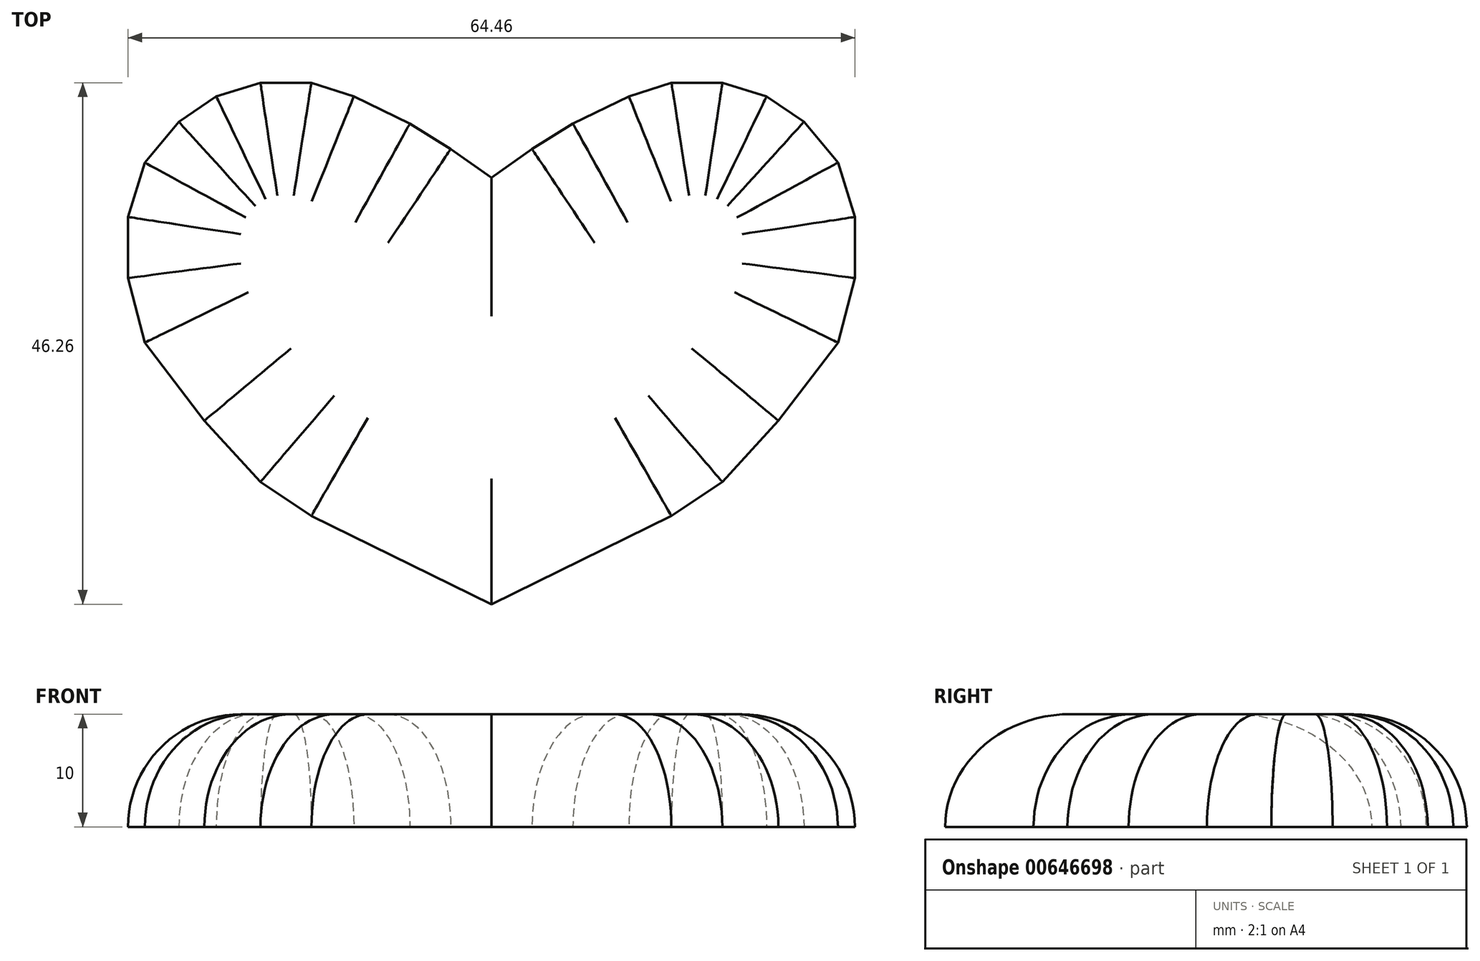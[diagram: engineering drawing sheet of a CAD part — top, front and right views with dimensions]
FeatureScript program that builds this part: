
annotation { "Feature Type Name" : "Feature", "Feature Type Description" : "" }
export const myFeature = defineFeature(function(context is Context, id is Id, definition is map)
    precondition{}
    {
        {
            var Q0;
            Q0=qCreatedBy(makeId("Top.planeOp"),FACE);
            var sketch = newSketch(context, id + "F0", { "sketchPlane" : qUnion([Q0])});
            skLineSegment(sketch, "E0", {"start": v(0, -24.58) * mm, "end": v(15.96, -16.75) * mm});
            skLineSegment(sketch, "E1", {"start": v(15.96, -16.75) * mm, "end": v(20.48, -13.73) * mm});
            skLineSegment(sketch, "E2", {"start": v(20.48, -13.73) * mm, "end": v(25.45, -8.31) * mm});
            skLineSegment(sketch, "E3", {"start": v(25.45, -8.31) * mm, "end": v(30.73, -1.38) * mm});
            skLineSegment(sketch, "E4", {"start": v(30.73, -1.38) * mm, "end": v(32.23, 4.35) * mm});
            skLineSegment(sketch, "E5", {"start": v(32.23, 4.35) * mm, "end": v(32.23, 9.77) * mm});
            skLineSegment(sketch, "E6", {"start": v(32.23, 9.77) * mm, "end": v(30.73, 14.6) * mm});
            skLineSegment(sketch, "E7", {"start": v(30.73, 14.6) * mm, "end": v(27.71, 18.2) * mm});
            skLineSegment(sketch, "E8", {"start": v(27.71, 18.2) * mm, "end": v(24.4, 20.47) * mm});
            skLineSegment(sketch, "E9", {"start": v(24.4, 20.47) * mm, "end": v(20.48, 21.68) * mm});
            skLineSegment(sketch, "E10", {"start": v(20.48, 21.68) * mm, "end": v(15.96, 21.68) * mm});
            skLineSegment(sketch, "E11", {"start": v(15.96, 21.68) * mm, "end": v(12.2, 20.47) * mm});
            skLineSegment(sketch, "E12", {"start": v(12.2, 20.47) * mm, "end": v(7.22, 18.06) * mm});
            skLineSegment(sketch, "E13", {"start": v(7.22, 18.06) * mm, "end": v(3.6, 15.8) * mm});
            skLineSegment(sketch, "E14", {"start": v(3.6, 15.8) * mm, "end": v(0, 13.24) * mm});
            skLineSegment(sketch, "E15", {"start": v(0, 13.24) * mm, "end": v(0, -24.58) * mm});
            skSolve(sketch);
        }
        {
            var Q0;
            Q0 = qSketchRegion(id + "F0", true);
            extrude(context, id + "F1", {"entities" : qUnion([Q0]), "depth" : 10 * mm, "offsetDistance" : 25.4 * mm});
        }
        {
            var Q0;
            Q0=makeQuery(id+"F1.opExtrude","SWEPT_BODY",BODY,{"disambiguationData":[OSD([sQuery(id+"F0.wireOp",EDGE,"E0"),sQuery(id+"F0.wireOp",EDGE,"E1"),sQuery(id+"F0.wireOp",EDGE,"E2"),sQuery(id+"F0.wireOp",EDGE,"E3"),sQuery(id+"F0.wireOp",EDGE,"E4"),sQuery(id+"F0.wireOp",EDGE,"E5"),sQuery(id+"F0.wireOp",EDGE,"E6"),sQuery(id+"F0.wireOp",EDGE,"E7"),sQuery(id+"F0.wireOp",EDGE,"E8"),sQuery(id+"F0.wireOp",EDGE,"E9"),sQuery(id+"F0.wireOp",EDGE,"E10"),sQuery(id+"F0.wireOp",EDGE,"E11"),sQuery(id+"F0.wireOp",EDGE,"E12"),sQuery(id+"F0.wireOp",EDGE,"E13"),sQuery(id+"F0.wireOp",EDGE,"E14"),sQuery(id+"F0.wireOp",EDGE,"E15")])]});
            var Q1;
            Q1=qCreatedBy(makeId("Right.planeOp"),FACE);
            mirror(context, id + "F2", {"operationType" : NewBodyOperationType.ADD, "entities" : qUnion([Q0]), "mirrorPlane" : qUnion([Q1])});
        }
        {
            var Q0;
            Q0=makeQuery(id+"F2.opPattern","COPY",EDGE,{"derivedFrom":makeQuery(id+"F1.opExtrude","CAP_EDGE",EDGE,{"disambiguationData":[OSD([sQuery(id+"F0.wireOp",EDGE,"E0")])],"isStart":false}),"instanceName":"1"});
            var Q1;
            Q1=makeQuery(id+"F1.opExtrude","CAP_EDGE",EDGE,{"disambiguationData":[OSD([sQuery(id+"F0.wireOp",EDGE,"E0")])],"isStart":false});
            var Q2;
            Q2=makeQuery(id+"F1.opExtrude","CAP_EDGE",EDGE,{"disambiguationData":[OSD([sQuery(id+"F0.wireOp",EDGE,"E1")])],"isStart":false});
            var Q3;
            Q3=makeQuery(id+"F1.opExtrude","CAP_EDGE",EDGE,{"disambiguationData":[OSD([sQuery(id+"F0.wireOp",EDGE,"E2")])],"isStart":false});
            var Q4;
            Q4=makeQuery(id+"F1.opExtrude","CAP_EDGE",EDGE,{"disambiguationData":[OSD([sQuery(id+"F0.wireOp",EDGE,"E3")])],"isStart":false});
            var Q5;
            Q5=makeQuery(id+"F1.opExtrude","CAP_EDGE",EDGE,{"disambiguationData":[OSD([sQuery(id+"F0.wireOp",EDGE,"E4")])],"isStart":false});
            var Q6;
            Q6=makeQuery(id+"F1.opExtrude","CAP_EDGE",EDGE,{"disambiguationData":[OSD([sQuery(id+"F0.wireOp",EDGE,"E5")])],"isStart":false});
            var Q7;
            Q7=makeQuery(id+"F1.opExtrude","CAP_EDGE",EDGE,{"disambiguationData":[OSD([sQuery(id+"F0.wireOp",EDGE,"E6")])],"isStart":false});
            var Q8;
            Q8=makeQuery(id+"F1.opExtrude","CAP_EDGE",EDGE,{"disambiguationData":[OSD([sQuery(id+"F0.wireOp",EDGE,"E7")])],"isStart":false});
            var Q9;
            Q9=makeQuery(id+"F1.opExtrude","CAP_EDGE",EDGE,{"disambiguationData":[OSD([sQuery(id+"F0.wireOp",EDGE,"E8")])],"isStart":false});
            var Q10;
            Q10=makeQuery(id+"F1.opExtrude","CAP_EDGE",EDGE,{"disambiguationData":[OSD([sQuery(id+"F0.wireOp",EDGE,"E9")])],"isStart":false});
            var Q11;
            Q11=makeQuery(id+"F1.opExtrude","CAP_EDGE",EDGE,{"disambiguationData":[OSD([sQuery(id+"F0.wireOp",EDGE,"E10")])],"isStart":false});
            var Q12;
            Q12=makeQuery(id+"F1.opExtrude","CAP_EDGE",EDGE,{"disambiguationData":[OSD([sQuery(id+"F0.wireOp",EDGE,"E11")])],"isStart":false});
            var Q13;
            Q13=makeQuery(id+"F1.opExtrude","CAP_EDGE",EDGE,{"disambiguationData":[OSD([sQuery(id+"F0.wireOp",EDGE,"E12")])],"isStart":false});
            var Q14;
            Q14=makeQuery(id+"F1.opExtrude","CAP_EDGE",EDGE,{"disambiguationData":[OSD([sQuery(id+"F0.wireOp",EDGE,"E14")])],"isStart":false});
            var Q15;
            Q15=makeQuery(id+"F1.opExtrude","CAP_EDGE",EDGE,{"disambiguationData":[OSD([sQuery(id+"F0.wireOp",EDGE,"E13")])],"isStart":false});
            var Q16;
            Q16=makeQuery(id+"F2.opPattern","COPY",EDGE,{"derivedFrom":makeQuery(id+"F1.opExtrude","CAP_EDGE",EDGE,{"disambiguationData":[OSD([sQuery(id+"F0.wireOp",EDGE,"E14")])],"isStart":false}),"instanceName":"1"});
            var Q17;
            Q17=makeQuery(id+"F2.opPattern","COPY",EDGE,{"derivedFrom":makeQuery(id+"F1.opExtrude","CAP_EDGE",EDGE,{"disambiguationData":[OSD([sQuery(id+"F0.wireOp",EDGE,"E13")])],"isStart":false}),"instanceName":"1"});
            var Q18;
            Q18=makeQuery(id+"F2.opPattern","COPY",EDGE,{"derivedFrom":makeQuery(id+"F1.opExtrude","CAP_EDGE",EDGE,{"disambiguationData":[OSD([sQuery(id+"F0.wireOp",EDGE,"E12")])],"isStart":false}),"instanceName":"1"});
            var Q19;
            Q19=makeQuery(id+"F2.opPattern","COPY",EDGE,{"derivedFrom":makeQuery(id+"F1.opExtrude","CAP_EDGE",EDGE,{"disambiguationData":[OSD([sQuery(id+"F0.wireOp",EDGE,"E11")])],"isStart":false}),"instanceName":"1"});
            var Q20;
            Q20=makeQuery(id+"F2.opPattern","COPY",EDGE,{"derivedFrom":makeQuery(id+"F1.opExtrude","CAP_EDGE",EDGE,{"disambiguationData":[OSD([sQuery(id+"F0.wireOp",EDGE,"E10")])],"isStart":false}),"instanceName":"1"});
            var Q21;
            Q21=makeQuery(id+"F2.opPattern","COPY",EDGE,{"derivedFrom":makeQuery(id+"F1.opExtrude","CAP_EDGE",EDGE,{"disambiguationData":[OSD([sQuery(id+"F0.wireOp",EDGE,"E9")])],"isStart":false}),"instanceName":"1"});
            var Q22;
            Q22=makeQuery(id+"F2.opPattern","COPY",EDGE,{"derivedFrom":makeQuery(id+"F1.opExtrude","CAP_EDGE",EDGE,{"disambiguationData":[OSD([sQuery(id+"F0.wireOp",EDGE,"E8")])],"isStart":false}),"instanceName":"1"});
            var Q23;
            Q23=makeQuery(id+"F2.opPattern","COPY",EDGE,{"derivedFrom":makeQuery(id+"F1.opExtrude","CAP_EDGE",EDGE,{"disambiguationData":[OSD([sQuery(id+"F0.wireOp",EDGE,"E7")])],"isStart":false}),"instanceName":"1"});
            var Q24;
            Q24=makeQuery(id+"F2.opPattern","COPY",EDGE,{"derivedFrom":makeQuery(id+"F1.opExtrude","CAP_EDGE",EDGE,{"disambiguationData":[OSD([sQuery(id+"F0.wireOp",EDGE,"E6")])],"isStart":false}),"instanceName":"1"});
            var Q25;
            Q25=makeQuery(id+"F2.opPattern","COPY",EDGE,{"derivedFrom":makeQuery(id+"F1.opExtrude","CAP_EDGE",EDGE,{"disambiguationData":[OSD([sQuery(id+"F0.wireOp",EDGE,"E5")])],"isStart":false}),"instanceName":"1"});
            var Q26;
            Q26=makeQuery(id+"F2.opPattern","COPY",EDGE,{"derivedFrom":makeQuery(id+"F1.opExtrude","CAP_EDGE",EDGE,{"disambiguationData":[OSD([sQuery(id+"F0.wireOp",EDGE,"E4")])],"isStart":false}),"instanceName":"1"});
            var Q27;
            Q27=makeQuery(id+"F2.opPattern","COPY",EDGE,{"derivedFrom":makeQuery(id+"F1.opExtrude","CAP_EDGE",EDGE,{"disambiguationData":[OSD([sQuery(id+"F0.wireOp",EDGE,"E3")])],"isStart":false}),"instanceName":"1"});
            var Q28;
            Q28=makeQuery(id+"F2.opPattern","COPY",EDGE,{"derivedFrom":makeQuery(id+"F1.opExtrude","CAP_EDGE",EDGE,{"disambiguationData":[OSD([sQuery(id+"F0.wireOp",EDGE,"E2")])],"isStart":false}),"instanceName":"1"});
            var Q29;
            Q29=makeQuery(id+"F2.opPattern","COPY",EDGE,{"derivedFrom":makeQuery(id+"F1.opExtrude","CAP_EDGE",EDGE,{"disambiguationData":[OSD([sQuery(id+"F0.wireOp",EDGE,"E1")])],"isStart":false}),"instanceName":"1"});
            fillet(context, id + "F3", {"entities" : qUnion([Q0, Q1, Q2, Q3, Q4, Q5, Q6, Q7, Q8, Q9, Q10, Q11, Q12, Q13, Q14, Q15, Q16, Q17, Q18, Q19, Q20, Q21, Q22, Q23, Q24, Q25, Q26, Q27, Q28, Q29]), "radius" : 10 * mm, "tangentPropagation" : true, "allowEdgeOverflow" : false});
        }
    });
